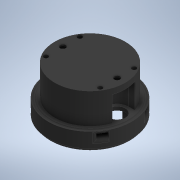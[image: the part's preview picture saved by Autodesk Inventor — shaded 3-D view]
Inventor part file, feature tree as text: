
AUTODESK INVENTOR PART (.ipt)
format: ipt  version: 2020 (Build 240168000, 168)  size: 489,472 bytes
history: native  units: in
note: dims shown in document units (in); Inventor stores cm internally (conversion verified against a paired STEP export)
features: sketch x11, extrude x8, revolve x2, hole x1, plane x1, fillet x1, projected_geometry x1
ambient origin geometry x8: Origin, YZ Plane, XZ Plane, XY Plane, X Axis, Y Axis, Z Axis, Center Point
bodies: Solid1 (feature_tree)
feature tree (25):
  revolve  "Revolution1"  [1 undecoded]
  hole  "Hole1"  [1 undecoded]
  revolve  "Revolution2"  [1 undecoded]
  extrude  "Extrusion2"  Depth=1.5in
  extrude  "Extrusion3"  Depth=0.125in
  extrude  "Extrusion4"  Depth=0.0312in
  extrude  "Extrusion8"  Depth=1.0in
  extrude  "Extrusion9"  Depth=2.4in
  extrude  "Extrusion11"  Depth=3.25in
  plane  "Work Plane3"
  extrude  "Extrusion12"  Depth=0.625in
  extrude  "Extrusion14"  Depth=0.125in TaperAngle=0.0deg
  fillet  "Fillet4"  Radius=1.0in
  sketch  "Sketch1"  dims[d1=0.6525in d2=1.5625in]
  sketch  "Sketch3"  dims[d4=90.0deg d13=1.75in]
  sketch  "Sketch5"  dims[d14=0.1in d15=0.125in]
  sketch  "Sketch6"  dims[d18=2.4in d19=1.5in]
  sketch  "Sketch7"  dims[d20=0.2031in d21=0.75in d22=0.3125in d23=0.875in d24=0.5635in d25=1.0in d26=0.0in d34=0.125in]
  projected_geometry  "Projected Loop1"
  sketch  "Sketch8"  dims[d35=1.75in d36=0.0312in]
  sketch  "Sketch13"  dims[d37=90.0deg d40=1.0in]
  sketch  "Sketch15"  dims[d41=1.0in d42=2.4in]
  sketch  "Sketch17"  dims[d43=1.875in d44=3.25in]
  sketch  "Sketch18"  dims[d45=0.625in d46=0.0in d47=0.25in]
  sketch  "Sketch20"  dims[d48=1.25in d49=0.0in d50=1.5in d51=0.0in d64=1.0in d65=2.4in d66=1.25in d67=0.0in d69=0.5in d70=0.188in d71=0.0in d76=2.0in d77=0.25in d78=0.0in d79=0.0in d80=-0.625in d82=0.375in d83=0.1875in d84=0.0in d88=0.125in d89=0.125in d91=1.25in d92=0.0in d93=0.125in]
note: 3 required parameter values undecoded (feature->parameter linkage not recoverable at this tier; creation-order binding heuristic only, values carry confidence <= 0.55)